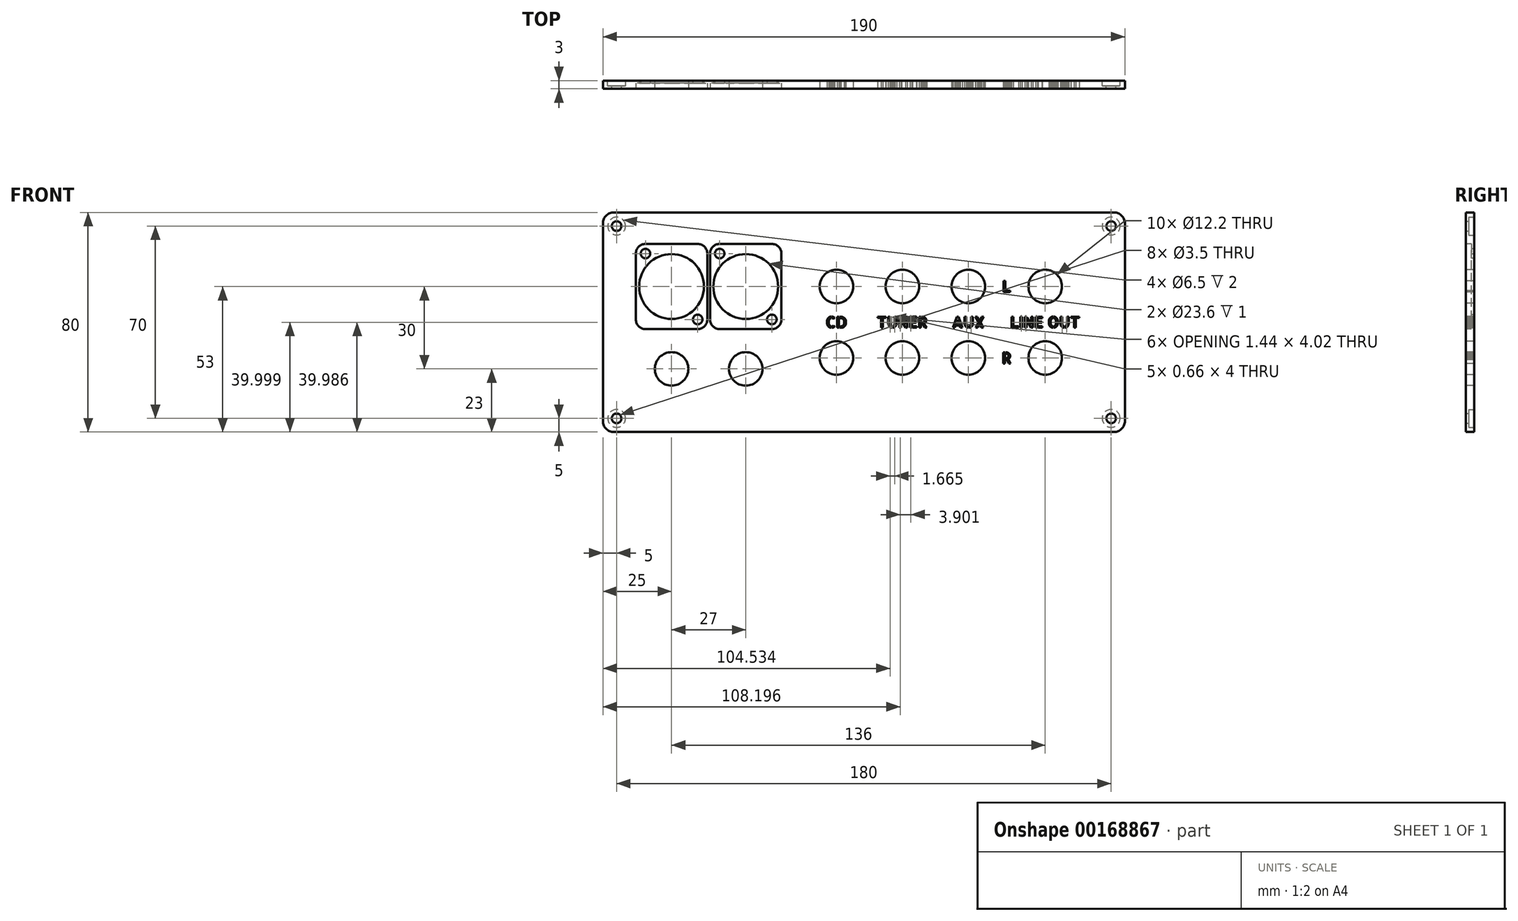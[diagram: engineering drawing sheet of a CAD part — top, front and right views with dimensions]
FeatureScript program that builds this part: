
annotation { "Feature Type Name" : "Feature", "Feature Type Description" : "" }
export const myFeature = defineFeature(function(context is Context, id is Id, definition is map)
    precondition{}
    {
        {
            var Q0;
            Q0=qCreatedBy(makeId("Front.planeOp"),FACE);
            var sketch = newSketch(context, id + "F0", { "sketchPlane" : qUnion([Q0])});
            skLineSegment(sketch, "E0.bottom", {"start": v(91, -40) * mm, "end": v(-91, -40) * mm});
            skLineSegment(sketch, "E0.top", {"start": v(91, 40) * mm, "end": v(-91, 40) * mm});
            skLineSegment(sketch, "E0.left", {"start": v(95, -36) * mm, "end": v(95, 36) * mm});
            skLineSegment(sketch, "E0.right", {"start": v(-95, -36) * mm, "end": v(-95, 36) * mm});
            skPoint(sketch, "E0.middle", {"position": v(0, 0) * mm});
            skLineSegment(sketch, "E1", {"start": v(-85.71, 13) * mm, "end": v(95.6, 13) * mm, "construction": true});
            skLineSegment(sketch, "E2", {"start": v(-95.37, 0) * mm, "end": v(94.03, 0) * mm, "construction": true});
            skLineSegment(sketch, "E3.MirrorCS", {"start": v(-85.71, -13) * mm, "end": v(95.6, -13) * mm, "construction": true});
            skLineSegment(sketch, "E4", {"start": v(-43, 41.44) * mm, "end": v(-43, -47.3) * mm, "construction": true});
            skLineSegment(sketch, "E5", {"start": v(-10, 39.64) * mm, "end": v(-10, -46.86) * mm, "construction": true});
            skLineSegment(sketch, "E6", {"start": v(38, 40.32) * mm, "end": v(38, -46.63) * mm, "construction": true});
            skLineSegment(sketch, "E7", {"start": v(66, 41.22) * mm, "end": v(66, -44.39) * mm, "construction": true});
            skCircle(sketch, "E8", {"center": v(-70, -17) * mm, "radius": 6.1 * mm});
            skCircle(sketch, "E9", {"center": v(-10, 13) * mm, "radius": 6.1 * mm});
            skCircle(sketch, "E10", {"center": v(14, 13) * mm, "radius": 6.1 * mm});
            skCircle(sketch, "E11", {"center": v(38, 13) * mm, "radius": 6.1 * mm});
            skCircle(sketch, "E12", {"center": v(66, 13) * mm, "radius": 6.1 * mm});
            skCircle(sketch, "E13", {"center": v(66, -13) * mm, "radius": 6.1 * mm});
            skCircle(sketch, "E14", {"center": v(38, -13) * mm, "radius": 6.1 * mm});
            skCircle(sketch, "E15", {"center": v(14, -13) * mm, "radius": 6.1 * mm});
            skCircle(sketch, "E16", {"center": v(-10, -13) * mm, "radius": 6.1 * mm});
            skCircle(sketch, "E17", {"center": v(-43, -17) * mm, "radius": 6.1 * mm});
            skPoint(sketch, "E18.visualSharp", {"position": v(-95, 40) * mm});
            skArc(sketch, "E18.filletArc", {"start": v(-91, 40) * mm, "mid": v(-93.83, 38.83) * mm, "end": v(-95, 36) * mm});
            skPoint(sketch, "E19.visualSharp", {"position": v(95, 40) * mm});
            skArc(sketch, "E19.filletArc", {"start": v(95, 36) * mm, "mid": v(93.83, 38.83) * mm, "end": v(91, 40) * mm});
            skPoint(sketch, "E20.visualSharp", {"position": v(95, -40) * mm});
            skArc(sketch, "E20.filletArc", {"start": v(91, -40) * mm, "mid": v(93.83, -38.83) * mm, "end": v(95, -36) * mm});
            skPoint(sketch, "E21.visualSharp", {"position": v(-95, -40) * mm});
            skArc(sketch, "E21.filletArc", {"start": v(-95, -36) * mm, "mid": v(-93.83, -38.83) * mm, "end": v(-91, -40) * mm});
            skLineSegment(sketch, "E22", {"start": v(14, 33.36) * mm, "end": v(14, -26.92) * mm, "construction": true});
            skLineSegment(sketch, "E23", {"start": v(-70, 17.5) * mm, "end": v(-70, -27.72) * mm, "construction": true});
            skCircle(sketch, "E24", {"center": v(-70, 13) * mm, "radius": 11.8 * mm});
            skLineSegment(sketch, "E25.bottom", {"start": v(-60.5, -2.5) * mm, "end": v(-79.5, -2.5) * mm});
            skLineSegment(sketch, "E25.top", {"start": v(-60.5, 28.5) * mm, "end": v(-79.5, 28.5) * mm});
            skLineSegment(sketch, "E25.left", {"start": v(-57, 1) * mm, "end": v(-57, 25) * mm});
            skLineSegment(sketch, "E25.right", {"start": v(-83, 1) * mm, "end": v(-83, 25) * mm});
            skLineSegment(sketch, "E26.bottom", {"start": v(-33.5, -2.5) * mm, "end": v(-52.5, -2.5) * mm});
            skLineSegment(sketch, "E26.top", {"start": v(-33.5, 28.5) * mm, "end": v(-52.5, 28.5) * mm});
            skLineSegment(sketch, "E26.left", {"start": v(-30, 1) * mm, "end": v(-30, 25) * mm});
            skLineSegment(sketch, "E26.right", {"start": v(-56, 1) * mm, "end": v(-56, 25) * mm});
            skPoint(sketch, "E26.middle", {"position": v(-43, 13) * mm});
            skCircle(sketch, "E27", {"center": v(-43, 13) * mm, "radius": 11.8 * mm});
            skPoint(sketch, "E28.visualSharp", {"position": v(-30, 28.5) * mm});
            skArc(sketch, "E28.filletArc", {"start": v(-30, 25) * mm, "mid": v(-31.03, 27.47) * mm, "end": v(-33.5, 28.5) * mm});
            skPoint(sketch, "E29.visualSharp", {"position": v(-56, 28.5) * mm});
            skArc(sketch, "E29.filletArc", {"start": v(-52.5, 28.5) * mm, "mid": v(-54.97, 27.47) * mm, "end": v(-56, 25) * mm});
            skPoint(sketch, "E30.visualSharp", {"position": v(-56, -2.5) * mm});
            skArc(sketch, "E30.filletArc", {"start": v(-56, 1) * mm, "mid": v(-54.97, -1.47) * mm, "end": v(-52.5, -2.5) * mm});
            skPoint(sketch, "E31.visualSharp", {"position": v(-30, -2.5) * mm});
            skArc(sketch, "E31.filletArc", {"start": v(-33.5, -2.5) * mm, "mid": v(-31.03, -1.47) * mm, "end": v(-30, 1) * mm});
            skPoint(sketch, "E32.visualSharp", {"position": v(-57, 28.5) * mm});
            skArc(sketch, "E32.filletArc", {"start": v(-57, 25) * mm, "mid": v(-58.03, 27.47) * mm, "end": v(-60.5, 28.5) * mm});
            skPoint(sketch, "E33.visualSharp", {"position": v(-83, 28.5) * mm});
            skArc(sketch, "E33.filletArc", {"start": v(-79.5, 28.5) * mm, "mid": v(-81.97, 27.47) * mm, "end": v(-83, 25) * mm});
            skPoint(sketch, "E34.visualSharp", {"position": v(-83, -2.5) * mm});
            skArc(sketch, "E34.filletArc", {"start": v(-83, 1) * mm, "mid": v(-81.97, -1.47) * mm, "end": v(-79.5, -2.5) * mm});
            skPoint(sketch, "E35.visualSharp", {"position": v(-57, -2.5) * mm});
            skArc(sketch, "E35.filletArc", {"start": v(-60.5, -2.5) * mm, "mid": v(-58.03, -1.47) * mm, "end": v(-57, 1) * mm});
            skLineSegment(sketch, "E36", {"start": v(-79.5, 31.15) * mm, "end": v(-79.5, -6.01) * mm, "construction": true});
            skLineSegment(sketch, "E37", {"start": v(-85.78, 25) * mm, "end": v(-56.54, 25) * mm, "construction": true});
            skLineSegment(sketch, "E38", {"start": v(-56.54, 25) * mm, "end": v(-28.92, 25) * mm, "construction": true});
            skLineSegment(sketch, "E39", {"start": v(-52.5, 30.05) * mm, "end": v(-52.5, -0.68) * mm, "construction": true});
            skLineSegment(sketch, "E40.MirrorCS", {"start": v(-60.5, 31.15) * mm, "end": v(-60.5, -6.01) * mm, "construction": true});
            skLineSegment(sketch, "E41.MirrorCS", {"start": v(-85.78, 1) * mm, "end": v(-56.54, 1) * mm, "construction": true});
            skLineSegment(sketch, "E42.MirrorCS", {"start": v(-56.54, 1) * mm, "end": v(-28.92, 1) * mm, "construction": true});
            skLineSegment(sketch, "E43.MirrorCS", {"start": v(-33.5, 30.05) * mm, "end": v(-33.5, -0.68) * mm, "construction": true});
            skLineSegment(sketch, "E44", {"start": v(-82.1, -17) * mm, "end": v(-31.97, -17) * mm, "construction": true});
            skSolve(sketch);
        }
        {
            var Q0;
            Q0 = qSketchRegion(id + "F0", true);
            var Q1;
            Q1=makeQuery(id+"F0.imprint","IMPRINT",FACE,{"disambiguationData":[TD([[makeQuery(id+"F0.imprint","IMPRINT",EDGE,{"derivedFrom":sQuery(id+"F0.wireOp",EDGE,"E24")}),-1.0]])]});
            var Q2;
            Q2=makeQuery(id+"F0.imprint","IMPRINT",FACE,{"disambiguationData":[TD([[makeQuery(id+"F0.imprint","IMPRINT",EDGE,{"derivedFrom":sQuery(id+"F0.wireOp",EDGE,"E26.bottom")}),-1.0]])]});
            extrude(context, id + "F1", {"entities" : qUnion([Q0, Q1, Q2]), "oppositeDirection" : true, "depth" : 3 * mm});
        }
        {
            var Q0;
            Q0=makeQuery(id+"F1.opExtrude","CAP_FACE",FACE,{"disambiguationData":[OSD([sQuery(id+"F0.wireOp",EDGE,"E0.bottom"),sQuery(id+"F0.wireOp",EDGE,"E0.top"),sQuery(id+"F0.wireOp",EDGE,"E0.left"),sQuery(id+"F0.wireOp",EDGE,"E0.right"),sQuery(id+"F0.wireOp",EDGE,"E8"),sQuery(id+"F0.wireOp",EDGE,"E9"),sQuery(id+"F0.wireOp",EDGE,"E10"),sQuery(id+"F0.wireOp",EDGE,"E11"),sQuery(id+"F0.wireOp",EDGE,"E12"),sQuery(id+"F0.wireOp",EDGE,"E13"),sQuery(id+"F0.wireOp",EDGE,"E14"),sQuery(id+"F0.wireOp",EDGE,"E15"),sQuery(id+"F0.wireOp",EDGE,"E16"),sQuery(id+"F0.wireOp",EDGE,"E17"),sQuery(id+"F0.wireOp",EDGE,"E18.filletArc"),sQuery(id+"F0.wireOp",EDGE,"E19.filletArc"),sQuery(id+"F0.wireOp",EDGE,"E20.filletArc"),sQuery(id+"F0.wireOp",EDGE,"E21.filletArc")])],"isStart":false});
            var sketch = newSketch(context, id + "F2", { "sketchPlane" : qUnion([Q0])});
            skLineSegment(sketch, "E45", {"start": v(-103.47, 35) * mm, "end": v(120, 35) * mm, "construction": true});
            skLineSegment(sketch, "E46", {"start": v(-90, 42.73) * mm, "end": v(-90, -48.6) * mm, "construction": true});
            skLineSegment(sketch, "E47.MirrorCS", {"start": v(90, 42.73) * mm, "end": v(90, -48.6) * mm, "construction": true});
            skLineSegment(sketch, "E48.MirrorCS", {"start": v(-103.47, -35) * mm, "end": v(120, -35) * mm, "construction": true});
            skPoint(sketch, "E49", {"position": v(-90, 35) * mm});
            skPoint(sketch, "E50", {"position": v(90, 35) * mm});
            skPoint(sketch, "E51", {"position": v(90, -35) * mm});
            skPoint(sketch, "E52", {"position": v(-90, -35) * mm});
            skSolve(sketch);
        }
        {
            var Q0;
            Q0=sQuery(id+"F2.wireOp",VERTEX,"E49");
            var Q1;
            Q1=sQuery(id+"F2.wireOp",VERTEX,"E50");
            var Q2;
            Q2=sQuery(id+"F2.wireOp",VERTEX,"E51");
            var Q3;
            Q3=sQuery(id+"F2.wireOp",VERTEX,"E52");
            var Q4;
            Q4=makeQuery(id+"F1.opExtrude","SWEPT_BODY",BODY,{"disambiguationData":[OSD([sQuery(id+"F0.wireOp",EDGE,"E0.bottom"),sQuery(id+"F0.wireOp",EDGE,"E0.top"),sQuery(id+"F0.wireOp",EDGE,"E0.left"),sQuery(id+"F0.wireOp",EDGE,"E0.right"),sQuery(id+"F0.wireOp",EDGE,"E8"),sQuery(id+"F0.wireOp",EDGE,"E9"),sQuery(id+"F0.wireOp",EDGE,"E10"),sQuery(id+"F0.wireOp",EDGE,"E11"),sQuery(id+"F0.wireOp",EDGE,"E12"),sQuery(id+"F0.wireOp",EDGE,"E13"),sQuery(id+"F0.wireOp",EDGE,"E14"),sQuery(id+"F0.wireOp",EDGE,"E15"),sQuery(id+"F0.wireOp",EDGE,"E16"),sQuery(id+"F0.wireOp",EDGE,"E17"),sQuery(id+"F0.wireOp",EDGE,"E18.filletArc"),sQuery(id+"F0.wireOp",EDGE,"E19.filletArc"),sQuery(id+"F0.wireOp",EDGE,"E20.filletArc"),sQuery(id+"F0.wireOp",EDGE,"E21.filletArc")])]});
            hole(context, id + "F3", {"style" : HoleStyle.C_BORE, "endStyle" : HoleEndStyle.THROUGH, "holeDiameter" : 3.5 * mm, "cBoreDiameter" : 6.5 * mm, "cBoreDepth" : 2 * mm, "startFromSketch" : true, "locations" : qUnion([Q0, Q1, Q2, Q3]), "scope" : qUnion([Q4]), "isTappedThrough" : true});
        }
        {
            var Q0;
            Q0=makeQuery(id+"F1.opExtrude","CAP_FACE",FACE,{"disambiguationData":[OSD([sQuery(id+"F0.wireOp",EDGE,"E0.bottom"),sQuery(id+"F0.wireOp",EDGE,"E0.top"),sQuery(id+"F0.wireOp",EDGE,"E0.left"),sQuery(id+"F0.wireOp",EDGE,"E0.right"),sQuery(id+"F0.wireOp",EDGE,"E8"),sQuery(id+"F0.wireOp",EDGE,"E9"),sQuery(id+"F0.wireOp",EDGE,"E10"),sQuery(id+"F0.wireOp",EDGE,"E11"),sQuery(id+"F0.wireOp",EDGE,"E12"),sQuery(id+"F0.wireOp",EDGE,"E13"),sQuery(id+"F0.wireOp",EDGE,"E14"),sQuery(id+"F0.wireOp",EDGE,"E15"),sQuery(id+"F0.wireOp",EDGE,"E16"),sQuery(id+"F0.wireOp",EDGE,"E17"),sQuery(id+"F0.wireOp",EDGE,"E18.filletArc"),sQuery(id+"F0.wireOp",EDGE,"E19.filletArc"),sQuery(id+"F0.wireOp",EDGE,"E20.filletArc"),sQuery(id+"F0.wireOp",EDGE,"E21.filletArc")])],"isStart":true});
            var sketch = newSketch(context, id + "F4", { "sketchPlane" : qUnion([Q0])});
            skLineSegment(sketch, "E53", {"start": v(-70, 25.45) * mm, "end": v(-70, -28.4) * mm, "construction": true});
            skLineSegment(sketch, "E54", {"start": v(-10, 30.05) * mm, "end": v(-10, -28.76) * mm, "construction": true});
            skLineSegment(sketch, "E55", {"start": v(14, 30.78) * mm, "end": v(14, -30.42) * mm, "construction": true});
            skLineSegment(sketch, "E56", {"start": v(38, 30.97) * mm, "end": v(38, -28.76) * mm, "construction": true});
            skLineSegment(sketch, "E57", {"start": v(66, 29.81) * mm, "end": v(66, -30.6) * mm, "construction": true});
            skLineSegment(sketch, "E58", {"start": v(52, 24.53) * mm, "end": v(52, -25.45) * mm, "construction": true});
            skLineSegment(sketch, "E59", {"start": v(38, -13) * mm, "end": v(66, -13) * mm, "construction": true});
            skLineSegment(sketch, "E60", {"start": v(38, 13) * mm, "end": v(66, 13) * mm, "construction": true});
            skText(sketch, "E61", { "text": "CD", "fontName": "AllertaStencil-Regular.ttf"});
            skText(sketch, "E62", { "text": "TUNER", "fontName": "AllertaStencil-Regular.ttf"});
            skText(sketch, "E63", { "text": "AUX", "fontName": "AllertaStencil-Regular.ttf"});
            skText(sketch, "E64", { "text": "L", "fontName": "AllertaStencil-Regular.ttf"});
            skText(sketch, "E65", { "text": "R", "fontName": "AllertaStencil-Regular.ttf"});
            skText(sketch, "E66", { "text": "LINE OUT", "fontName": "AllertaStencil-Regular.ttf"});
            const initialGuessF4  = {"E61": [-0.01388, -0.002, 1, 0, 0.004], "E62": [0.00477, -0.002, 1, 0, 0.004], "E63": [0.03205, -0.002, 1, 0, 0.004], "E64": [0.05031, 0.011, 1, 0, 0.004], "E65": [0.05021, -0.015, 1, 0, 0.004], "E66": [0.05326, -0.002, 1, 0, 0.004]};
            skSetInitialGuess(sketch, initialGuessF4);
            skSolve(sketch);
        }
        {
            var Q0;
            Q0 = qSketchRegion(id + "F4", true);
            extrude(context, id + "F5", {"entities" : qUnion([Q0]), "operationType" : NewBodyOperationType.REMOVE, "endBound" : BoundingType.THROUGH_ALL, "oppositeDirection" : true, "depth" : 0.3 * mm});
        }
        {
            var Q0;
            Q0=makeQuery(id+"F0.imprint","IMPRINT",FACE,{"disambiguationData":[TD([[makeQuery(id+"F0.imprint","IMPRINT",EDGE,{"derivedFrom":sQuery(id+"F0.wireOp",EDGE,"E24")}),-1.0]])]});
            var Q1;
            Q1=makeQuery(id+"F0.imprint","IMPRINT",FACE,{"disambiguationData":[TD([[makeQuery(id+"F0.imprint","IMPRINT",EDGE,{"derivedFrom":sQuery(id+"F0.wireOp",EDGE,"E26.bottom")}),-1.0]])]});
            extrude(context, id + "F6", {"entities" : qUnion([Q0, Q1]), "operationType" : NewBodyOperationType.REMOVE, "oppositeDirection" : true, "depth" : 2 * mm});
        }
        {
            var Q0;
            Q0=sQuery(id+"F0.wireOp",VERTEX,"E33.filletArc.center");
            var Q1;
            Q1=sQuery(id+"F0.wireOp",VERTEX,"E35.filletArc.center");
            var Q2;
            Q2=sQuery(id+"F0.wireOp",VERTEX,"E29.filletArc.center");
            var Q3;
            Q3=sQuery(id+"F0.wireOp",VERTEX,"E31.filletArc.center");
            var Q4;
            Q4=makeQuery(id+"F1.opExtrude","SWEPT_BODY",BODY,{"disambiguationData":[OSD([sQuery(id+"F0.wireOp",EDGE,"E0.bottom"),sQuery(id+"F0.wireOp",EDGE,"E0.top"),sQuery(id+"F0.wireOp",EDGE,"E0.left"),sQuery(id+"F0.wireOp",EDGE,"E0.right"),sQuery(id+"F0.wireOp",EDGE,"E8"),sQuery(id+"F0.wireOp",EDGE,"E9"),sQuery(id+"F0.wireOp",EDGE,"E10"),sQuery(id+"F0.wireOp",EDGE,"E11"),sQuery(id+"F0.wireOp",EDGE,"E12"),sQuery(id+"F0.wireOp",EDGE,"E13"),sQuery(id+"F0.wireOp",EDGE,"E14"),sQuery(id+"F0.wireOp",EDGE,"E15"),sQuery(id+"F0.wireOp",EDGE,"E16"),sQuery(id+"F0.wireOp",EDGE,"E17"),sQuery(id+"F0.wireOp",EDGE,"E18.filletArc"),sQuery(id+"F0.wireOp",EDGE,"E19.filletArc"),sQuery(id+"F0.wireOp",EDGE,"E20.filletArc"),sQuery(id+"F0.wireOp",EDGE,"E21.filletArc"),sQuery(id+"F0.wireOp",EDGE,"E24"),sQuery(id+"F0.wireOp",EDGE,"E27")])]});
            hole(context, id + "F7", {"style" : HoleStyle.SIMPLE, "endStyle" : HoleEndStyle.THROUGH, "holeDiameter" : 3.5 * mm, "locations" : qUnion([Q0, Q1, Q2, Q3]), "scope" : qUnion([Q4]), "isTappedThrough" : true});
        }
    });
